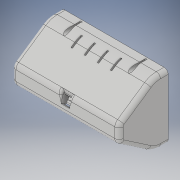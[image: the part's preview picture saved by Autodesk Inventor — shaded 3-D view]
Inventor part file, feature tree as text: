
AUTODESK INVENTOR PART (.ipt)
format: ipt  version: 2018 (Build 220112000, 112)  size: 765,440 bytes
history: native  units: in
note: dims shown in document units (in); Inventor stores cm internally (conversion verified against a paired STEP export)
features: extrude x20, sketch x19, fillet x11, chamfer x5, plane x3, draft x2, shell x1
ambient origin geometry x8: Origin, YZ Plane, XZ Plane, XY Plane, X Axis, Y Axis, Z Axis, Center Point
bodies: Solid1 (feature_tree)
feature tree (61):
  extrude  "Extrusion1"  Depth=3.5in
  shell  "Shell1"  Thickness=0.5in
  extrude  "Extrusion2"  Depth=7.6772in TaperAngle=0.0deg
  fillet  "Fillet4"  Radius=0.25in
  fillet  "Fillet5"  Radius=0.25in
  fillet  "Fillet6"  Radius=0.25in
  plane  "Work Plane1"
  extrude  "Extrusion3"  Depth=7.6772in TaperAngle=0.0deg
  extrude  "Extrusion4"  Depth=1.0in
  extrude  "Extrusion5"  Depth=0.315in
  extrude  "Extrusion6"  TaperAngle=90.0deg  [1 undecoded]
  plane  "Work Plane2"
  fillet  "Fillet13"  Radius=0.5157in
  fillet  "Fillet14"  Radius=0.6496in
  extrude  "Extrusion8"  Depth=1.0in TaperAngle=0.0deg
  extrude  "Extrusion9"  Depth=0.6496in
  extrude  "Extrusion10"  Depth=0.5in
  extrude  "Extrusion11"  Depth=0.5in
  extrude  "Extrusion12"  Depth=0.5709in TaperAngle=0.0deg
  chamfer  "Chamfer4"  Distance=0.2756in
  extrude  "Extrusion13"  Depth=0.1969in
  plane  "Work Plane3"
  extrude  "Extrusion15"  Depth=6.5in
  extrude  "Extrusion16"  Depth=0.125in TaperAngle=0.0deg
  fillet  "Fillet15"  Radius=0.25in
  chamfer  "Chamfer5"  Distance=0.125in
  extrude  "Extrusion17"  Depth=0.1181in
  fillet  "Fillet16"  Radius=0.1181in
  extrude  "Extrusion22"  Depth=0.5in TaperAngle=0.0deg
  extrude  "Extrusion23"  Depth=0.1181in
  fillet  "Fillet22"  Radius=0.7874in
  fillet  "Fillet23"  Radius=0.5in
  chamfer  "Chamfer7"  Distance=0.7874in
  fillet  "Fillet24"  Radius=1.0in
  fillet  "Fillet25"  Radius=0.1181in
  chamfer  "Chamfer9"  Distance=0.7874in
  chamfer  "Chamfer10"  Distance=1.0in
  extrude  "Extrusion27"  Depth=0.1181in
  extrude  "Extrusion28"  Depth=0.7874in
  draft  "FaceDraft1"
  draft  "FaceDraft2"
  extrude  "Extrusion14"  Depth=0.0394in
  sketch  "Sketch1"  dims[d0=4.4094in d1=3.5in d2=0.5in]
  sketch  "Sketch2"  dims[d3=0.5in d4=7.6772in d5=0.0in d6=0.25in d7=0.25in d8=0.25in]
  sketch  "Sketch4"  dims[d10=0.25in d11=7.6772in d12=0.0in]
  sketch  "Sketch5"  dims[d13=1.0in d14=1.0in]
  sketch  "Sketch6"  dims[d18=0.4724in d19=0.315in]
  sketch  "Sketch8"  dims[d20=1.5748in d21=90.0deg d22=0.5157in d23=0.6496in]
  sketch  "Sketch9"  dims[d24=0.1969in d25=1.0in d26=0.0in]
  sketch  "Sketch10"  dims[d27=0.5157in d28=0.6496in]
  sketch  "Sketch11"  dims[d29=0.2362in d30=0.5in]
  sketch  "Sketch12"  dims[d31=0.125in d32=0.5in]
  sketch  "Sketch13"  dims[d33=0.5709in d34=0.0in d35=0.5709in d36=0.0in d37=0.2756in d38=0.0in]
  sketch  "Sketch14"  dims[d44=0.8in d60=0.1969in]
  sketch  "Sketch15"  dims[d61=0.1181in d62=6.5in]
  sketch  "Sketch16"  dims[d63=2.5in d64=0.125in d65=0.0in d66=0.25in]
  sketch  "Sketch17"  dims[d67=0.25in d68=0.125in d69=0.0in]
  sketch  "Sketch23"  dims[d70=0.1181in d71=0.1181in d72=0.1181in]
  sketch  "Sketch25"  dims[d73=0.1181in d74=0.5in d75=0.0in]
  sketch  "Sketch29"  dims[d76=0.5in d77=0.1181in d78=0.7874in d79=0.5in]
  sketch  "Sketch30"  dims[d80=0.1181in d81=0.7874in d82=1.0in d83=0.1181in d84=0.7874in d85=1.0in d86=0.1181in d87=0.7874in d88=0.0394in d89=1.0in d90=0.0in d91=0.25in d92=0.0in d93=2.3622in d94=1.0in d95=0.1575in d96=0.0in d97=0.1575in d98=0.125in d99=45.0deg d100=1.2894in d101=4.9606in d102=0.1181in d103=0.1181in d104=0.1181in d105=0.1181in d106=2.0in d107=0.0in d108=-1.5in d109=0.2756in d110=0.2756in d111=0.2756in d112=0.2756in d113=1.378in d114=0.0in d115=0.0in d116=2.3622in d117=1.5748in d118=0.1575in d119=0.0in d120=0.6102in d121=0.2657in d122=0.0787in d123=0.0787in d124=0.0787in d125=0.0787in d126=0.1969in d127=0.1969in d128=0.1969in d129=0.1969in d130=0.1181in d131=0.0in d132=0.0787in d133=0.1575in d134=0.125in d135=45.0deg d136=0.0787in d138=1.136in d139=0.2568in d140=0.2568in d141=0.2362in d142=0.0in d149=0.1181in d150=0.1181in d153=0.2362in d154=0.0in d159=0.0in d161=0.0in d162=3.0in d163=0.0in d164=0.2362in d168=0.2028in d170=0.0787in d171=0.0197in d172=0.315in d173=0.125in d174=45.0deg d178=0.0in d179=0.1969in d180=0.1969in d181=0.0in d182=0.0787in d183=0.125in d184=45.0deg d185=0.0787in d186=0.125in d187=45.0deg d197=0.8661in d198=0.1181in d199=0.0in d200=0.8661in d201=0.1181in d202=0.0in d203=-0.0344in d204=-0.0344in d205=0.9646in d206=1.3583in d207=0.4823in d208=0.4823in d209=0.6791in d210=0.6791in]
note: 1 required parameter value undecoded (feature->parameter linkage not recoverable at this tier; creation-order binding heuristic only, values carry confidence <= 0.55)
